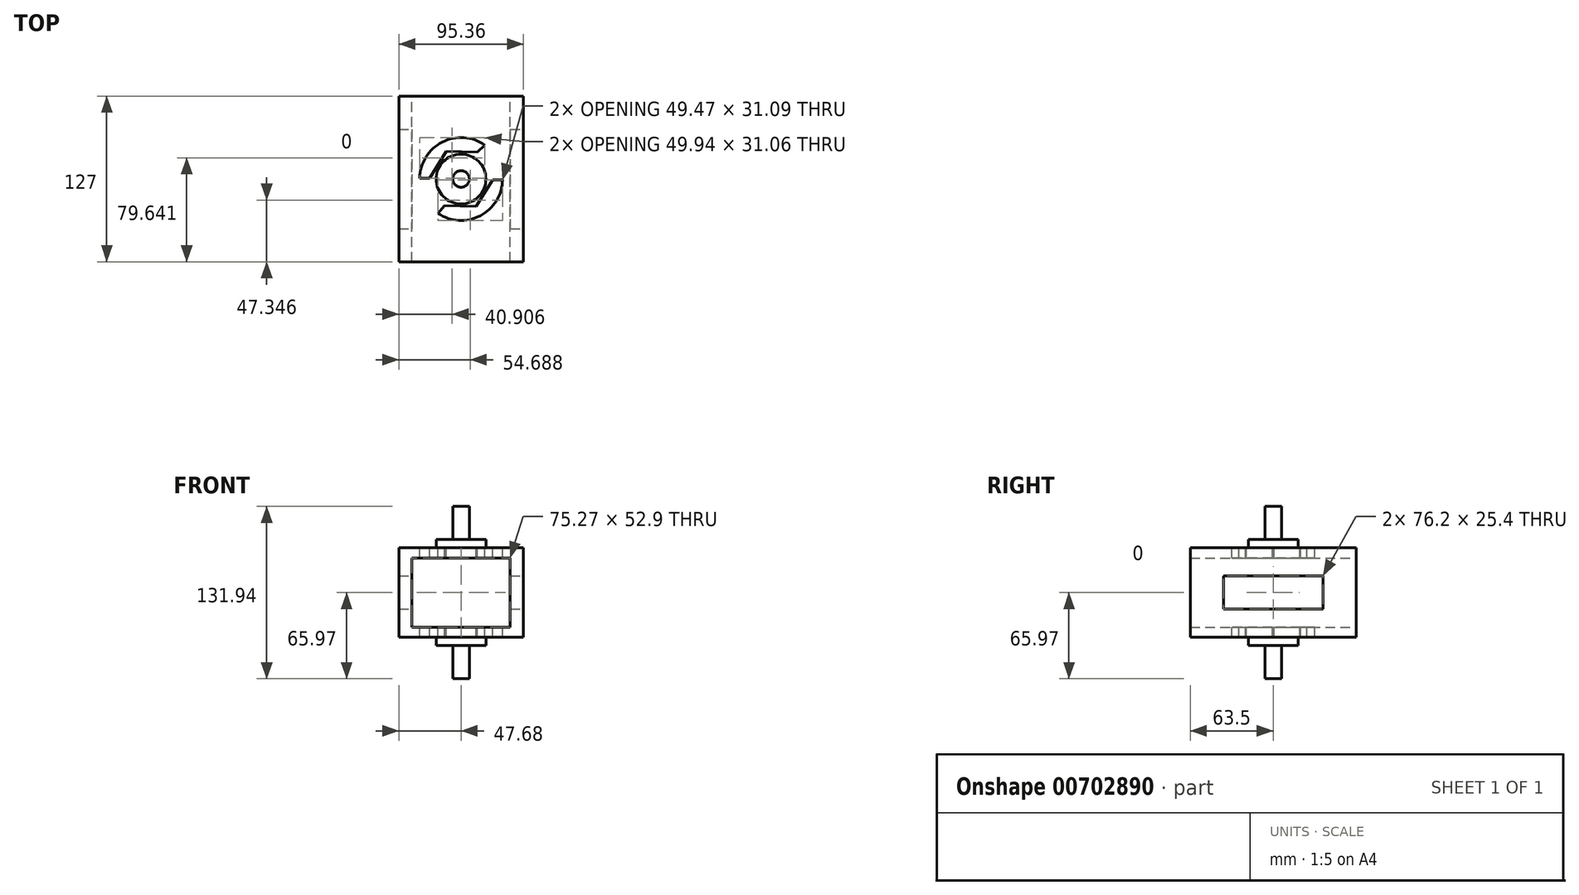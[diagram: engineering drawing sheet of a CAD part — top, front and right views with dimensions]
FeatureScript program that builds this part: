
annotation { "Feature Type Name" : "Feature", "Feature Type Description" : "" }
export const myFeature = defineFeature(function(context is Context, id is Id, definition is map)
    precondition{}
    {
        {
            var Q0;
            Q0=qCreatedBy(makeId("Front.planeOp"),FACE);
            var sketch = newSketch(context, id + "F0", { "sketchPlane" : qUnion([Q0])});
            skLineSegment(sketch, "E0.bottom", {"start": v(47.68, 34.22) * mm, "end": v(-47.68, 34.22) * mm});
            skLineSegment(sketch, "E0.top", {"start": v(47.68, -34.22) * mm, "end": v(-47.68, -34.22) * mm});
            skLineSegment(sketch, "E0.left", {"start": v(47.68, 34.22) * mm, "end": v(47.68, -34.22) * mm});
            skLineSegment(sketch, "E0.right", {"start": v(-47.68, 34.22) * mm, "end": v(-47.68, -34.22) * mm});
            skPoint(sketch, "E0.middle", {"position": v(0, 0) * mm});
            skLineSegment(sketch, "E1.bottom", {"start": v(37.64, 26.45) * mm, "end": v(-37.64, 26.45) * mm});
            skLineSegment(sketch, "E1.top", {"start": v(37.64, -26.45) * mm, "end": v(-37.64, -26.45) * mm});
            skLineSegment(sketch, "E1.left", {"start": v(37.64, 26.45) * mm, "end": v(37.64, -26.45) * mm});
            skLineSegment(sketch, "E1.right", {"start": v(-37.64, 26.45) * mm, "end": v(-37.64, -26.45) * mm});
            skSolve(sketch);
        }
        {
            var Q0;
            Q0=makeQuery(id+"F0.imprint","IMPRINT",FACE,{"disambiguationData":[TD([[makeQuery(id+"F0.imprint","IMPRINT",EDGE,{"derivedFrom":sQuery(id+"F0.wireOp",EDGE,"E0.bottom")}),1.0]])]});
            extrude(context, id + "F1", {"entities" : qUnion([Q0]), "endBound" : BoundingType.SYMMETRIC, "depth" : 127 * mm, "offsetDistance" : 25.4 * mm});
        }
        {
            var Q0;
            Q0=makeQuery(id+"F1.opExtrude","SWEPT_FACE",FACE,{"disambiguationData":[OSD([sQuery(id+"F0.wireOp",EDGE,"E0.bottom")])]});
            var sketch = newSketch(context, id + "F2", { "sketchPlane" : qUnion([Q0])});
            skCircle(sketch, "E2", {"center": v(0, 0) * mm, "radius": 31.75 * mm});
            skCircle(sketch, "E3.cCircle", {"center": v(0, 0) * mm, "radius": 20.83 * mm, "construction": true});
            skLineSegment(sketch, "E3.0", {"start": v(12.55, 20.52) * mm, "end": v(24.04, -0.6) * mm});
            skLineSegment(sketch, "E3.1", {"start": v(24.04, -0.6) * mm, "end": v(11.5, -21.13) * mm});
            skLineSegment(sketch, "E3.2", {"start": v(11.5, -21.13) * mm, "end": v(-12.55, -20.52) * mm});
            skLineSegment(sketch, "E3.3", {"start": v(-12.55, -20.52) * mm, "end": v(-24.04, 0.6) * mm});
            skLineSegment(sketch, "E3.4", {"start": v(-24.04, 0.6) * mm, "end": v(-11.5, 21.13) * mm});
            skLineSegment(sketch, "E3.5", {"start": v(-11.5, 21.13) * mm, "end": v(12.55, 20.52) * mm});
            skPoint(sketch, "E3.0.midPoint", {"position": v(18.3, 9.95) * mm});
            skLineSegment(sketch, "E4", {"start": v(-24.04, 0.6) * mm, "end": v(-31.74, 0.6) * mm});
            skLineSegment(sketch, "E5", {"start": v(-11.5, 21.13) * mm, "end": v(-15.71, 27.59) * mm});
            skLineSegment(sketch, "E6", {"start": v(12.55, 20.52) * mm, "end": v(18.2, 26.02) * mm});
            skLineSegment(sketch, "E7", {"start": v(-12.55, -20.52) * mm, "end": v(-17.73, -26.34) * mm});
            skLineSegment(sketch, "E8", {"start": v(11.5, -21.13) * mm, "end": v(15.28, -27.83) * mm});
            skLineSegment(sketch, "E9", {"start": v(24.04, -0.6) * mm, "end": v(31.74, -0.6) * mm});
            skSolve(sketch);
        }
        {
            var Q0;
            Q0=makeQuery(id+"F2.imprint","IMPRINT",FACE,{"disambiguationData":[TD([[makeQuery(id+"F2.imprint","IMPRINT",EDGE,{"derivedFrom":sQuery(id+"F2.wireOp",EDGE,"E3.5")}),1.0]])]});
            var Q1;
            Q1=makeQuery(id+"F2.imprint","IMPRINT",FACE,{"disambiguationData":[TD([[makeQuery(id+"F2.imprint","IMPRINT",EDGE,{"derivedFrom":sQuery(id+"F2.wireOp",EDGE,"E3.4")}),1.0]])]});
            var Q2;
            Q2=makeQuery(id+"F2.imprint","IMPRINT",FACE,{"disambiguationData":[TD([[makeQuery(id+"F2.imprint","IMPRINT",EDGE,{"derivedFrom":sQuery(id+"F2.wireOp",EDGE,"E3.2")}),1.0]])]});
            var Q3;
            Q3=makeQuery(id+"F2.imprint","IMPRINT",FACE,{"disambiguationData":[TD([[makeQuery(id+"F2.imprint","IMPRINT",EDGE,{"derivedFrom":sQuery(id+"F2.wireOp",EDGE,"E3.1")}),1.0]])]});
            extrude(context, id + "F3", {"entities" : qUnion([Q0, Q1, Q2, Q3]), "operationType" : NewBodyOperationType.REMOVE, "endBound" : BoundingType.THROUGH_ALL, "oppositeDirection" : true, "depth" : 25.4 * mm, "offsetDistance" : 25.4 * mm});
        }
        {
            var Q0;
            Q0=makeQuery(id+"F1.opExtrude","SWEPT_FACE",FACE,{"disambiguationData":[OSD([sQuery(id+"F0.wireOp",EDGE,"E0.bottom")])]});
            var sketch = newSketch(context, id + "F4", { "sketchPlane" : qUnion([Q0])});
            skCircle(sketch, "E10", {"center": v(0, 0) * mm, "radius": 19.05 * mm});
            skSolve(sketch);
        }
        {
            var Q0;
            Q0 = qSketchRegion(id + "F4", true);
            extrude(context, id + "F5", {"entities" : qUnion([Q0]), "operationType" : NewBodyOperationType.ADD, "depth" : 6.35 * mm, "offsetDistance" : 25.4 * mm});
        }
        {
            var Q0;
            Q0=makeQuery(id+"F1.opExtrude","SWEPT_FACE",FACE,{"disambiguationData":[OSD([sQuery(id+"F0.wireOp",EDGE,"E0.top")])]});
            var sketch = newSketch(context, id + "F6", { "sketchPlane" : qUnion([Q0])});
            skCircle(sketch, "E11", {"center": v(0, 0) * mm, "radius": 19.05 * mm});
            skSolve(sketch);
        }
        {
            var Q0;
            Q0 = qSketchRegion(id + "F6", true);
            extrude(context, id + "F7", {"entities" : qUnion([Q0]), "operationType" : NewBodyOperationType.ADD, "depth" : 6.35 * mm, "offsetDistance" : 25.4 * mm});
        }
        {
            var Q0;
            Q0=makeQuery(id+"F1.opExtrude","SWEPT_FACE",FACE,{"disambiguationData":[OSD([sQuery(id+"F0.wireOp",EDGE,"E0.left")])]});
            var sketch = newSketch(context, id + "F8", { "sketchPlane" : qUnion([Q0])});
            skLineSegment(sketch, "E12.bottom", {"start": v(38.1, 12.7) * mm, "end": v(-38.1, 12.7) * mm});
            skLineSegment(sketch, "E12.top", {"start": v(38.1, -12.7) * mm, "end": v(-38.1, -12.7) * mm});
            skLineSegment(sketch, "E12.left", {"start": v(38.1, 12.7) * mm, "end": v(38.1, -12.7) * mm});
            skLineSegment(sketch, "E12.right", {"start": v(-38.1, 12.7) * mm, "end": v(-38.1, -12.7) * mm});
            skPoint(sketch, "E12.middle", {"position": v(0, 0) * mm});
            skSolve(sketch);
        }
        {
            var Q0;
            Q0 = qSketchRegion(id + "F8", true);
            extrude(context, id + "F9", {"entities" : qUnion([Q0]), "operationType" : NewBodyOperationType.REMOVE, "endBound" : BoundingType.THROUGH_ALL, "oppositeDirection" : true, "depth" : 25.4 * mm, "offsetDistance" : 25.4 * mm});
        }
        {
            var Q0;
            Q0=makeQuery(id+"F5.opExtrude","CAP_FACE",FACE,{"disambiguationData":[OSD([sQuery(id+"F4.wireOp",EDGE,"E10")])],"isStart":false});
            var sketch = newSketch(context, id + "F10", { "sketchPlane" : qUnion([Q0])});
            skCircle(sketch, "E13", {"center": v(0, 0) * mm, "radius": 6.35 * mm});
            skSolve(sketch);
        }
        {
            var Q0;
            Q0 = qSketchRegion(id + "F10", true);
            extrude(context, id + "F11", {"entities" : qUnion([Q0]), "operationType" : NewBodyOperationType.ADD, "depth" : 25.4 * mm, "offsetDistance" : 25.4 * mm});
        }
        {
            var Q0;
            Q0=makeQuery(id+"F7.opExtrude","CAP_FACE",FACE,{"disambiguationData":[OSD([sQuery(id+"F6.wireOp",EDGE,"E11")])],"isStart":false});
            var sketch = newSketch(context, id + "F12", { "sketchPlane" : qUnion([Q0])});
            skCircle(sketch, "E14", {"center": v(0, 0) * mm, "radius": 6.35 * mm});
            skSolve(sketch);
        }
        {
            var Q0;
            Q0 = qSketchRegion(id + "F12", true);
            extrude(context, id + "F13", {"entities" : qUnion([Q0]), "operationType" : NewBodyOperationType.ADD, "depth" : 25.4 * mm, "offsetDistance" : 25.4 * mm});
        }
    });
